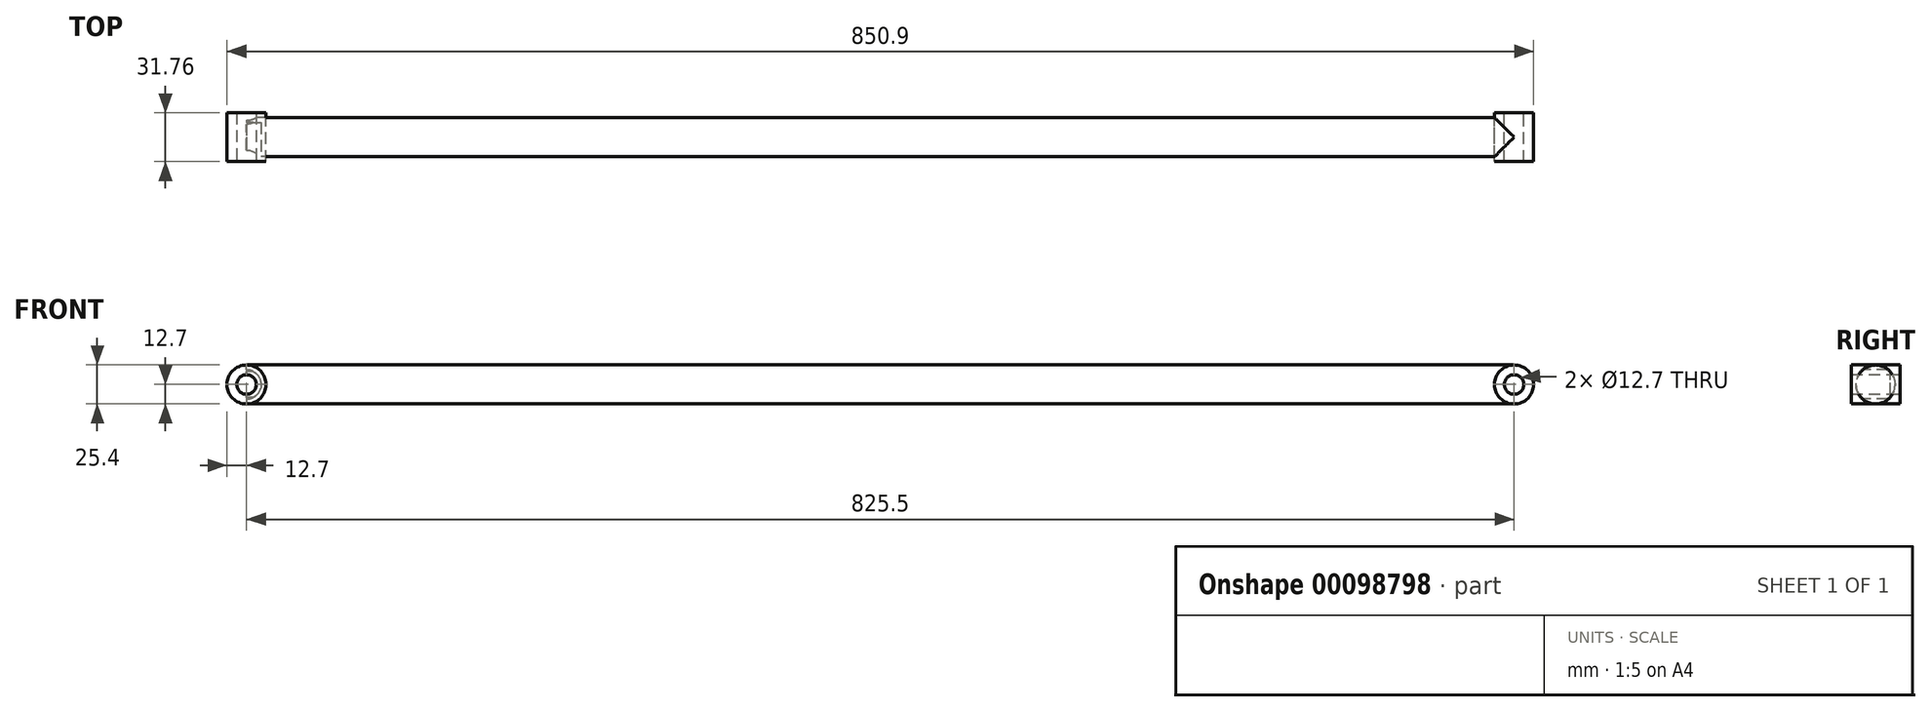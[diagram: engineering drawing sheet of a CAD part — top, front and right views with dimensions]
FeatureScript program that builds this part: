
annotation { "Feature Type Name" : "Feature", "Feature Type Description" : "" }
export const myFeature = defineFeature(function(context is Context, id is Id, definition is map)
    precondition{}
    {
        {
            var Q0;
            Q0=qCreatedBy(makeId("Front.planeOp"),FACE);
            var sketch = newSketch(context, id + "F0", { "sketchPlane" : qUnion([Q0])});
            skCircle(sketch, "E0", {"center": v(825.5, 0) * mm, "radius": 6.35 * mm});
            skLineSegment(sketch, "E1", {"start": v(0, 0) * mm, "end": v(825.5, 0) * mm});
            skCircle(sketch, "E2", {"center": v(0, 0) * mm, "radius": 12.7 * mm});
            skCircle(sketch, "E3", {"center": v(825.5, 0) * mm, "radius": 12.7 * mm});
            skSolve(sketch);
        }
        {
            var Q0;
            Q0 = qSketchRegion(id + "F0", true);
            extrude(context, id + "F1", {"entities" : qUnion([Q0]), "depth" : 31.75 * mm, "symmetric" : true});
        }
        {
            var Q0;
            Q0=qCreatedBy(makeId("Right.planeOp"),FACE);
            var sketch = newSketch(context, id + "F2", { "sketchPlane" : qUnion([Q0])});
            skCircle(sketch, "E4", {"center": v(0, 0) * mm, "radius": 12.7 * mm});
            skSolve(sketch);
        }
        {
            var Q0;
            Q0 = qSketchRegion(id + "F2", true);
            var Q1;
            Q1=sQuery(id+"F2.wireOp",EDGE,"E4");
            var Q2;
            Q2=makeQuery(id+"F1.opExtrude","SWEPT_FACE",FACE,{"disambiguationData":[OSD([sQuery(id+"F0.wireOp",EDGE,"E3")])]});
            extrude(context, id + "F3", {"entities" : qUnion([Q0]), "surfaceEntities" : qUnion([Q1]), "endBound" : BoundingType.UP_TO_SURFACE, "endBoundEntityFace" : qUnion([Q2]), "depth" : 1016 * mm});
        }
        {
            var Q0;
            Q0=makeQuery(id+"F1.opExtrude","CAP_FACE",FACE,{"disambiguationData":[OSD([sQuery(id+"F0.wireOp",EDGE,"oEOMtwuP-hSFr-Zsiy-xIcu-gxlsd7xaxkSq"),sQuery(id+"F0.wireOp",EDGE,"E2")])],"isStart":false});
            var sketch = newSketch(context, id + "F4", { "sketchPlane" : qUnion([Q0])});
            skCircle(sketch, "E5", {"center": v(0, 0) * mm, "radius": 9.53 * mm});
            skSolve(sketch);
        }
        {
            var Q0;
            Q0 = qSketchRegion(id + "F4", true);
            extrude(context, id + "F5", {"entities" : qUnion([Q0]), "oppositeDirection" : true, "depth" : 25.4 * mm});
        }
        {
            var Q0;
            Q0=makeQuery(id+"F5.opExtrude","SWEPT_BODY",BODY,{"disambiguationData":[OSD([sQuery(id+"F4.wireOp",EDGE,"E5")])]});
            var Q1;
            Q1=makeQuery(id+"F3.opExtrude","SWEPT_BODY",BODY,{"disambiguationData":[OSD([sQuery(id+"F2.wireOp",EDGE,"E4")])]});
            booleanBodies(context, id + "F6", {"operationType" : BooleanOperationType.SUBTRACTION, "tools" : qUnion([Q0]), "targets" : qUnion([Q1])});
        }
        {
            var Q0;
            Q0=makeQuery(id+"F1.opExtrude","CAP_FACE",FACE,{"disambiguationData":[OSD([sQuery(id+"F0.wireOp",EDGE,"E2")])],"isStart":false});
            var sketch = newSketch(context, id + "F7", { "sketchPlane" : qUnion([Q0])});
            skCircle(sketch, "E6", {"center": v(0, 0) * mm, "radius": 6.35 * mm});
            skSolve(sketch);
        }
        {
            var Q0;
            Q0 = qSketchRegion(id + "F7", true);
            extrude(context, id + "F8", {"entities" : qUnion([Q0]), "operationType" : NewBodyOperationType.REMOVE, "oppositeDirection" : true, "depth" : 50.8 * mm});
        }
    });
